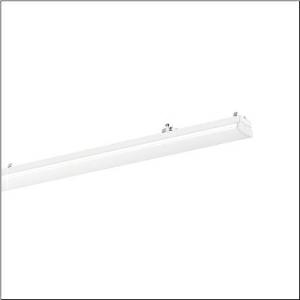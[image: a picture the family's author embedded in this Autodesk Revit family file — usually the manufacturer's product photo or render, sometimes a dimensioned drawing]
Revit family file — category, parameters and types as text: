
# Revit family: licross_21_recessed_opal_mo_52tl1d7n48xg
name_source: partatom
category: Lighting Fixtures
units: mm (PartAtom-declared; Revit-internal decimal feet)

## family parameters
Cut with Voids When Loaded = No
Host = Face
Light Source = No
Part Type = Normal
Room Calculation Point = No
Round Connector Dimension = Use Diameter
Shared = No

## types (1)
- Licross 21 recessed opal MO (1 x LED, 8360 lm, 47.9 W, 4000K)
    Apparent Load = 48 VA
    CIE Flux Codes = 44 73 91 87 100
    Color Rendering = 80
    Color Temperature = 4000K
    Default Elevation = 1800 mm
    Description = Licross 21 recessed opal MO, luminaire insert, of sheet steel, galvanised, coil coated, white, length: 1.500mm, width: 66mm, height: 67mm, LED rated luminous flux: 8.360lm, light colour: 840, SDCM (Standard Deviation of Colour Matching)MacAdam ≤ 3 SDCM (initial), control gear: ON/OFF, with plug, 3-pole, with phase selection, mains connection: 220..240V, AC, 50/60Hz, rated input power: 48W, internal wiring halogen-free, primary optical cover: cover, of PMMA, light emission: direct with ceiling illumination distribution, primary light characteristic: symmetric, protection rating (complete): IP40, insulation class (complete): insulation class I (protective earthing), certification: CE, ENEC, VDE, UKCA, protection symbol: D if used in an environment without relevant dust loads with corresponding accessories, impact resistance: IK06, permissible ambient temperature for indoor applications: -35..+40°C, corresponds to IFS (International Featured Standards) requirements for safety and quality in the food industry, reducing of maximum allowable ambient temperature of 5°C with ceiling mounting, LABS conformity tested according to VDMA 24364:2018-05, The light source and the operating device comply with the requirements of the Ecodesign Regulation (EU) 2019/2020 and are replaceable in accordance with this regulation, packaging unit: 1 piece
    Height = 83 mm
    Lamp = 1 x LED
    Lamp Light Flux = 8360 lm
    Lamp Power = 47.9 W
    Lamp count = 1
    Length = 1500 mm
    Luminous efficacy = 175 lm/W
    Manufacturer = Siteco
    ModVariant = No
    Model = 52TL1D7N48XG
    Mounting Place = Ceiling
    Mounting Type = Pendant
    Number of Poles = 1
    OnlyDefault = Yes
    Power Factor = 1
    Product Name = Licross 21 recessed opal MO
    Product group = luminaire insert | ceiling pendant
    ProductGroupID = 901
    Protection Class = Protection class I
    Protection Degree = IP 40
    RLX_Detail_Level = 1
    RLX_Emergency_Light_Flux = 0 lm
    RLX_Emergency_Type = 0
    RLX_Emergency_Type_DB = No
    RlxData = <blob elided: 23357 chars, md5=379c7736>
    Socket = socket
    Standby Power = 0 W
    System Light Flux = 8360 lm
    System Power = 48 W
    Type Comments = Product without accessories
    Type Image = l_1313666.jpg
    URL = http://relux.com
    VarID = ---
    Voltage = 0 V
    Weight = 0.00 kg
    Width = 76 mm

## geometry (parser evidence)
native form markers: Blend x4, Sweep x13
no freeform markers — native parametric forms only
